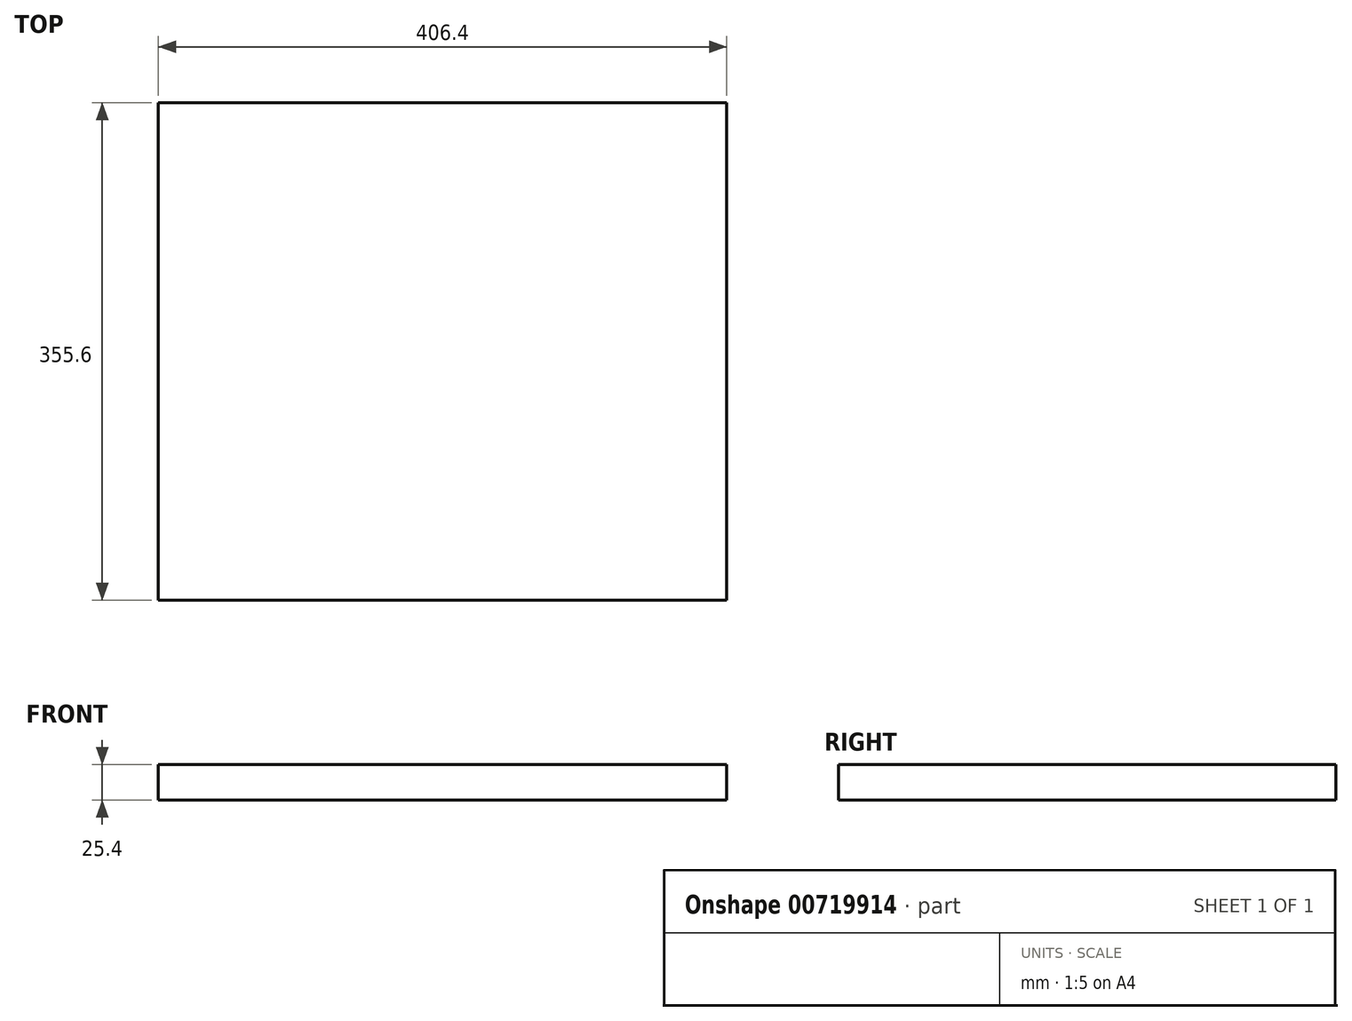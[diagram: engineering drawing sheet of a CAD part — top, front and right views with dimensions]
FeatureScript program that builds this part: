
annotation { "Feature Type Name" : "Feature", "Feature Type Description" : "" }
export const myFeature = defineFeature(function(context is Context, id is Id, definition is map)
    precondition{}
    {
        {
            var Q0;
            Q0=qCreatedBy(makeId("Top.planeOp"),FACE);
            var sketch = newSketch(context, id + "F0", { "sketchPlane" : qUnion([Q0])});
            skLineSegment(sketch, "E0.bottom", {"start": v(-271.12, 236.1) * mm, "end": v(135.28, 236.1) * mm});
            skLineSegment(sketch, "E0.top", {"start": v(-271.12, -119.5) * mm, "end": v(135.28, -119.5) * mm});
            skLineSegment(sketch, "E0.left", {"start": v(-271.12, 236.1) * mm, "end": v(-271.12, -119.5) * mm});
            skLineSegment(sketch, "E0.right", {"start": v(135.28, 236.1) * mm, "end": v(135.28, -119.5) * mm});
            skSolve(sketch);
        }
        {
            var Q0;
            Q0=makeQuery(id+"F0.imprint","IMPRINT",FACE,{"disambiguationData":[TD([[makeQuery(id+"F0.imprint","IMPRINT",EDGE,{"derivedFrom":sQuery(id+"F0.wireOp",EDGE,"E0.bottom")}),-1.0]])]});
            extrude(context, id + "F1", {"entities" : qUnion([Q0]), "depth" : 25.4 * mm, "offsetDistance" : 25.4 * mm});
        }
    });
